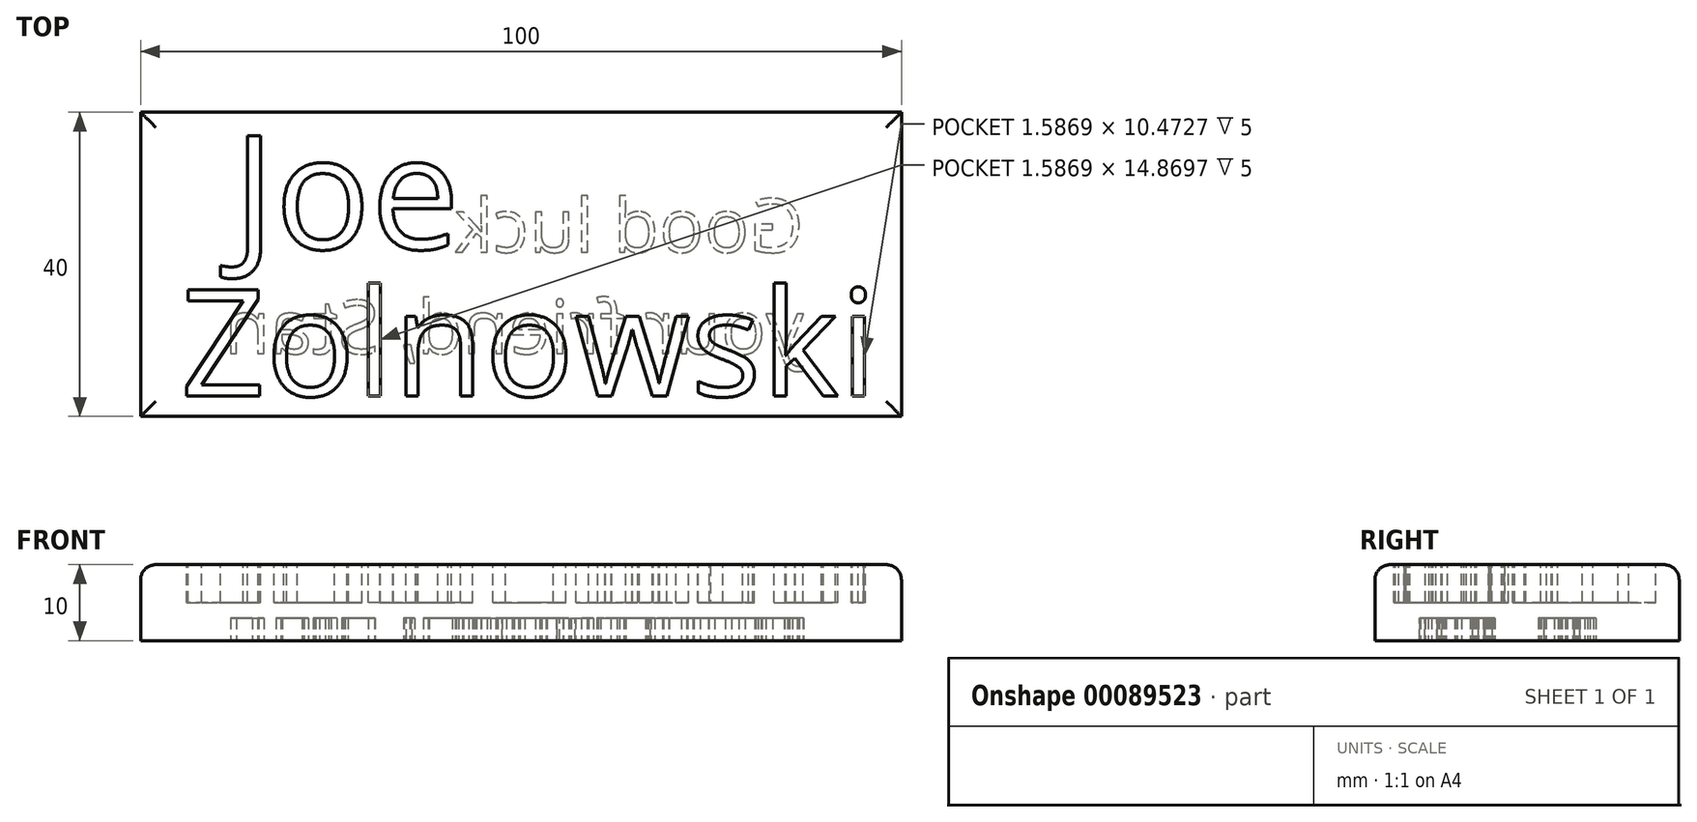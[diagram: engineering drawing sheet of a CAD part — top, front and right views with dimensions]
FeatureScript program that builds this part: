
annotation { "Feature Type Name" : "Feature", "Feature Type Description" : "" }
export const myFeature = defineFeature(function(context is Context, id is Id, definition is map)
    precondition{}
    {
        {
            var Q0;
            Q0=qCreatedBy(makeId("Top.planeOp"),FACE);
            var sketch = newSketch(context, id + "F0", { "sketchPlane" : qUnion([Q0])});
            skLineSegment(sketch, "E0.bottom", {"start": v(50, -20) * mm, "end": v(-50, -20) * mm});
            skLineSegment(sketch, "E0.top", {"start": v(50, 20) * mm, "end": v(-50, 20) * mm});
            skLineSegment(sketch, "E0.left", {"start": v(50, -20) * mm, "end": v(50, 20) * mm});
            skLineSegment(sketch, "E0.right", {"start": v(-50, -20) * mm, "end": v(-50, 20) * mm});
            skPoint(sketch, "E0.middle", {"position": v(0, 0) * mm});
            skSolve(sketch);
        }
        {
            var Q0;
            Q0 = qSketchRegion(id + "F0", true);
            extrude(context, id + "F1", {"entities" : qUnion([Q0]), "depth" : 10 * mm});
        }
        {
            var Q0;
            Q0=makeQuery(id+"F1.opExtrude","CAP_FACE",FACE,{"disambiguationData":[OSD([sQuery(id+"F0.wireOp",EDGE,"E0.bottom"),sQuery(id+"F0.wireOp",EDGE,"E0.top"),sQuery(id+"F0.wireOp",EDGE,"E0.left"),sQuery(id+"F0.wireOp",EDGE,"E0.right")])],"isStart":false});
            var sketch = newSketch(context, id + "F2", { "sketchPlane" : qUnion([Q0])});
            skText(sketch, "E1", { "text": "Joe", "fontName": "OpenSans-Regular.ttf"});
            skText(sketch, "E2", { "text": "Zolnowski\n", "fontName": "OpenSans-Regular.ttf"});
            skCircle(sketch, "E3", {"center": v(5.7, 9.8) * mm, "radius": 3.42 * mm});
            skCircle(sketch, "E4", {"center": v(20.86, 7.26) * mm, "radius": 3.74 * mm});
            skCircle(sketch, "E5", {"center": v(31.06, 14.51) * mm, "radius": 3.62 * mm});
            skLineSegment(sketch, "E6", {"start": v(5.7, 9.8) * mm, "end": v(20.86, 7.26) * mm});
            skLineSegment(sketch, "E7", {"start": v(20.86, 7.26) * mm, "end": v(31.06, 14.51) * mm});
            const initialGuessF2  = {"E1": [-0.03789, 0.00202, 1, 0, 0.015], "E2": [-0.04475, -0.01732, 1, 0, 0.01409]};
            skSetInitialGuess(sketch, initialGuessF2);
            skSolve(sketch);
        }
        {
            var Q0;
            Q0=makeQuery(id+"F2.imprint","IMPRINT",FACE,{"disambiguationData":[TD([[makeQuery(id+"F2.imprint","IMPRINT",EDGE,{"derivedFrom":sQuery(id+"F2.wireOp",EDGE,"E1.sketch_text.stroke-0")}),-1.0]])]});
            var Q1;
            Q1=makeQuery(id+"F2.imprint","IMPRINT",FACE,{"disambiguationData":[TD([[makeQuery(id+"F2.imprint","IMPRINT",EDGE,{"derivedFrom":sQuery(id+"F2.wireOp",EDGE,"E2.sketch_text.stroke-0")}),-1.0]])]});
            var Q2;
            Q2=makeQuery(id+"F2.imprint","IMPRINT",FACE,{"disambiguationData":[TD([[makeQuery(id+"F2.imprint","IMPRINT",EDGE,{"derivedFrom":sQuery(id+"F2.wireOp",EDGE,"E2.sketch_text.stroke-27")}),-1.0]])]});
            var Q3;
            Q3=makeQuery(id+"F2.imprint","IMPRINT",FACE,{"disambiguationData":[TD([[makeQuery(id+"F2.imprint","IMPRINT",EDGE,{"derivedFrom":sQuery(id+"F2.wireOp",EDGE,"E2.sketch_text.stroke-31")}),-1.0]])]});
            var Q4;
            Q4=makeQuery(id+"F2.imprint","IMPRINT",FACE,{"disambiguationData":[TD([[makeQuery(id+"F2.imprint","IMPRINT",EDGE,{"derivedFrom":sQuery(id+"F2.wireOp",EDGE,"E2.sketch_text.stroke-65")}),-1.0]])]});
            var Q5;
            Q5=makeQuery(id+"F2.imprint","IMPRINT",FACE,{"disambiguationData":[TD([[makeQuery(id+"F2.imprint","IMPRINT",EDGE,{"derivedFrom":sQuery(id+"F2.wireOp",EDGE,"E2.sketch_text.stroke-88")}),-1.0]])]});
            var Q6;
            Q6=makeQuery(id+"F2.imprint","IMPRINT",FACE,{"disambiguationData":[TD([[makeQuery(id+"F2.imprint","IMPRINT",EDGE,{"derivedFrom":sQuery(id+"F2.wireOp",EDGE,"E2.sketch_text.stroke-113")}),-1.0]])]});
            var Q7;
            Q7=makeQuery(id+"F2.imprint","IMPRINT",FACE,{"disambiguationData":[TD([[makeQuery(id+"F2.imprint","IMPRINT",EDGE,{"derivedFrom":sQuery(id+"F2.wireOp",EDGE,"E2.sketch_text.stroke-128")}),-1.0]])]});
            var Q8;
            Q8=makeQuery(id+"F2.imprint","IMPRINT",FACE,{"disambiguationData":[TD([[makeQuery(id+"F2.imprint","IMPRINT",EDGE,{"derivedFrom":sQuery(id+"F2.wireOp",EDGE,"E2.sketch_text.stroke-132")}),-1.0]])]});
            var Q9;
            Q9=makeQuery(id+"F2.imprint","IMPRINT",FACE,{"disambiguationData":[TD([[makeQuery(id+"F2.imprint","IMPRINT",EDGE,{"derivedFrom":sQuery(id+"F2.wireOp",EDGE,"E1.sketch_text.stroke-10")}),-1.0]])]});
            var Q10;
            Q10=makeQuery(id+"F2.imprint","IMPRINT",FACE,{"disambiguationData":[TD([[makeQuery(id+"F2.imprint","IMPRINT",EDGE,{"derivedFrom":sQuery(id+"F2.wireOp",EDGE,"E1.sketch_text.stroke-27")}),-1.0]])]});
            var Q11;
            Q11=makeQuery(id+"F2.imprint","IMPRINT",FACE,{"disambiguationData":[TD([[makeQuery(id+"F2.imprint","IMPRINT",EDGE,{"derivedFrom":sQuery(id+"F2.wireOp",EDGE,"E2.sketch_text.stroke-10")}),-1.0]])]});
            var Q12;
            Q12=makeQuery(id+"F2.imprint","IMPRINT",FACE,{"disambiguationData":[TD([[makeQuery(id+"F2.imprint","IMPRINT",EDGE,{"derivedFrom":sQuery(id+"F2.wireOp",EDGE,"E2.sketch_text.stroke-48")}),-1.0]])]});
            extrude(context, id + "F3", {"entities" : qUnion([Q0, Q1, Q2, Q3, Q4, Q5, Q6, Q7, Q8, Q9, Q10, Q11, Q12]), "operationType" : NewBodyOperationType.REMOVE, "oppositeDirection" : true, "depth" : 5 * mm});
        }
        {
            var Q0;
            Q0=makeQuery(id+"F1.opExtrude","CAP_EDGE",EDGE,{"disambiguationData":[OSD([sQuery(id+"F0.wireOp",EDGE,"E0.top")])],"isStart":false});
            var Q1;
            Q1=makeQuery(id+"F1.opExtrude","CAP_EDGE",EDGE,{"disambiguationData":[OSD([sQuery(id+"F0.wireOp",EDGE,"E0.right")])],"isStart":false});
            var Q2;
            Q2=makeQuery(id+"F1.opExtrude","CAP_EDGE",EDGE,{"disambiguationData":[OSD([sQuery(id+"F0.wireOp",EDGE,"E0.bottom")])],"isStart":false});
            var Q3;
            Q3=makeQuery(id+"F1.opExtrude","CAP_EDGE",EDGE,{"disambiguationData":[OSD([sQuery(id+"F0.wireOp",EDGE,"E0.left")])],"isStart":false});
            fillet(context, id + "F4", {"entities" : qUnion([Q0, Q1, Q2, Q3]), "radius" : 2 * mm, "tangentPropagation" : true, "allowEdgeOverflow" : false});
        }
        {
            var Q0;
            Q0=makeQuery(id+"F1.opExtrude","CAP_FACE",FACE,{"disambiguationData":[OSD([sQuery(id+"F0.wireOp",EDGE,"E0.bottom"),sQuery(id+"F0.wireOp",EDGE,"E0.top"),sQuery(id+"F0.wireOp",EDGE,"E0.left"),sQuery(id+"F0.wireOp",EDGE,"E0.right")])],"isStart":true});
            var sketch = newSketch(context, id + "F5", { "sketchPlane" : qUnion([Q0])});
            skText(sketch, "E8", { "text": "Good luck\nyour friend, Stan", "fontName": "OpenSans-Regular.ttf"});
            const initialGuessF5  = {"E8": [0.03715, -0.0016, -1, 0, 0.00707]};
            skSetInitialGuess(sketch, initialGuessF5);
            skSolve(sketch);
        }
        {
            var Q0;
            Q0 = qSketchRegion(id + "F5", true);
            extrude(context, id + "F6", {"entities" : qUnion([Q0]), "operationType" : NewBodyOperationType.REMOVE, "oppositeDirection" : true, "depth" : 3 * mm});
        }
    });
